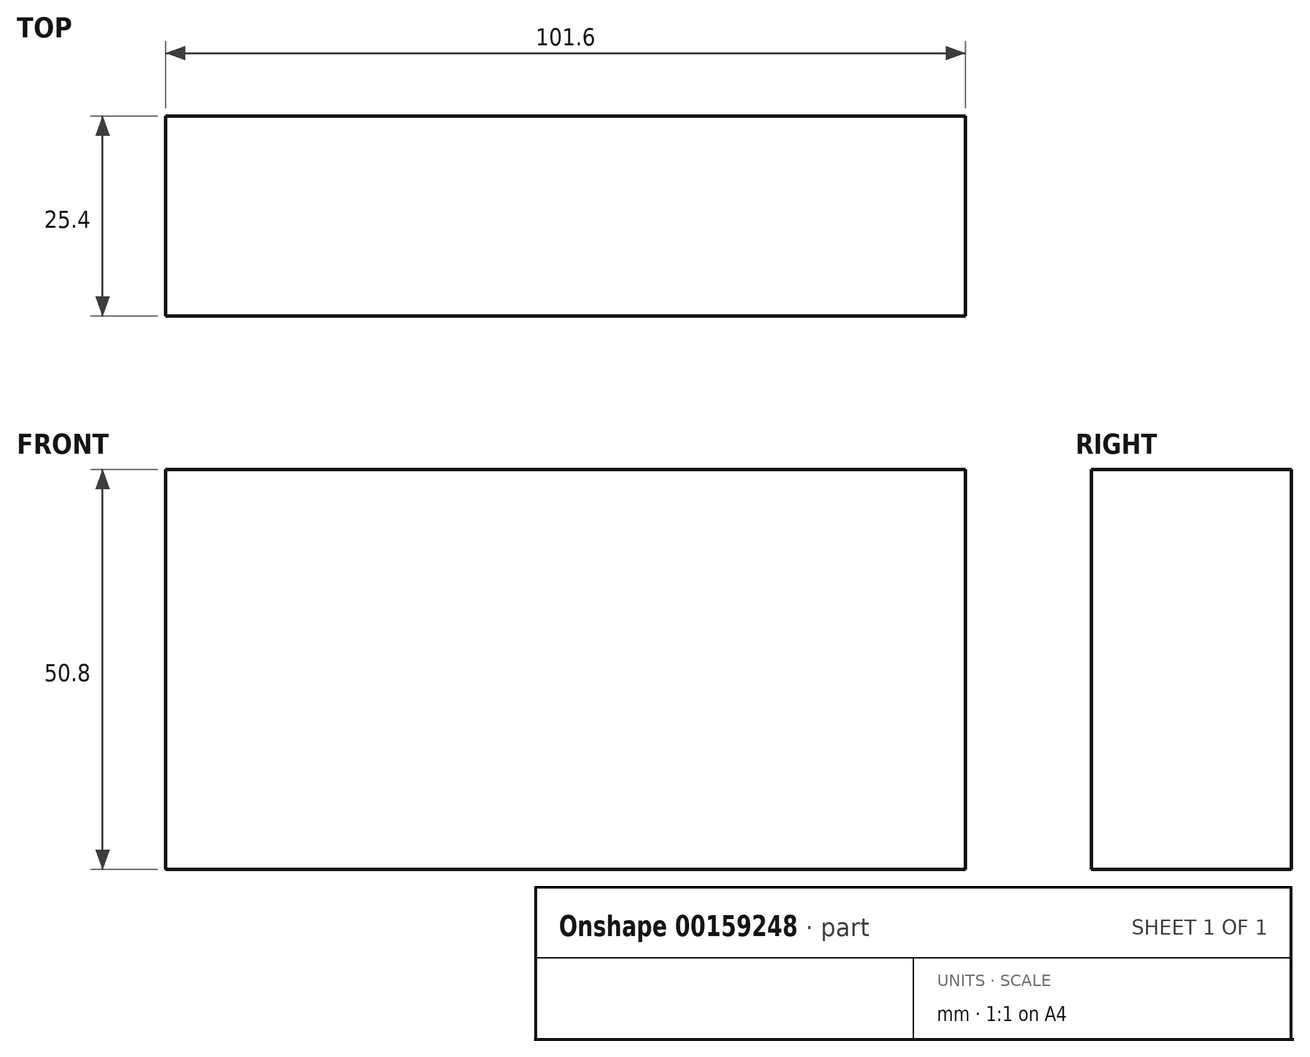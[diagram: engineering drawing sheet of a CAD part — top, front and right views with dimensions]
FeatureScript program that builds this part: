
annotation { "Feature Type Name" : "Feature", "Feature Type Description" : "" }
export const myFeature = defineFeature(function(context is Context, id is Id, definition is map)
    precondition{}
    {
        {
            var Q0;
            Q0=qCreatedBy(makeId("Front.planeOp"),FACE);
            var sketch = newSketch(context, id + "F0", { "sketchPlane" : qUnion([Q0])});
            skLineSegment(sketch, "E0.bottom", {"start": v(50.8, 25.4) * mm, "end": v(-50.8, 25.4) * mm});
            skLineSegment(sketch, "E0.top", {"start": v(50.8, -25.4) * mm, "end": v(-50.8, -25.4) * mm});
            skLineSegment(sketch, "E0.left", {"start": v(50.8, 25.4) * mm, "end": v(50.8, -25.4) * mm});
            skLineSegment(sketch, "E0.right", {"start": v(-50.8, 25.4) * mm, "end": v(-50.8, -25.4) * mm});
            skPoint(sketch, "E0.middle", {"position": v(0, 0) * mm});
            skSolve(sketch);
        }
        {
            var Q0;
            Q0 = qSketchRegion(id + "F0", true);
            extrude(context, id + "F1", {"entities" : qUnion([Q0]), "depth" : 25.4 * mm});
        }
    });
